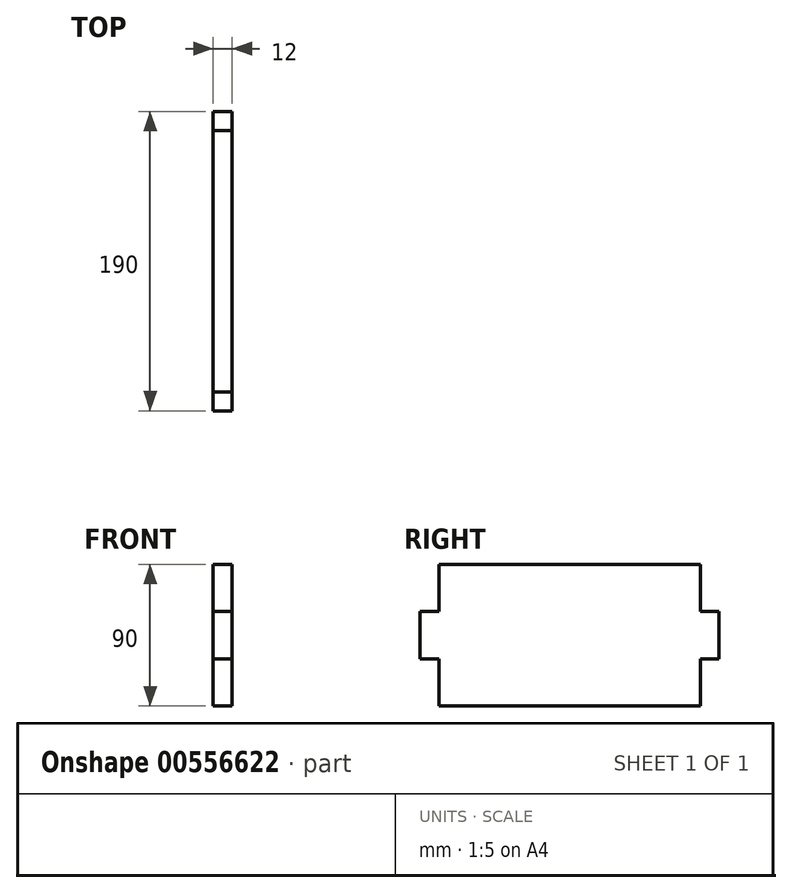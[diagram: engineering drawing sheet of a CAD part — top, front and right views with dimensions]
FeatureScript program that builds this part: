
annotation { "Feature Type Name" : "Feature", "Feature Type Description" : "" }
export const myFeature = defineFeature(function(context is Context, id is Id, definition is map)
    precondition{}
    {
        {
            var Q0;
            Q0=qCreatedBy(makeId("Right.planeOp"),FACE);
            var sketch = newSketch(context, id + "F0", { "sketchPlane" : qUnion([Q0])});
            skLineSegment(sketch, "E0", {"start": v(0, 0) * mm, "end": v(0, 30) * mm});
            skLineSegment(sketch, "E1", {"start": v(0, 30) * mm, "end": v(-12, 30) * mm});
            skLineSegment(sketch, "E2", {"start": v(-12, 30) * mm, "end": v(-12, 60) * mm});
            skLineSegment(sketch, "E3", {"start": v(-12, 60) * mm, "end": v(0, 60) * mm});
            skLineSegment(sketch, "E4", {"start": v(0, 60) * mm, "end": v(0, 90) * mm});
            skLineSegment(sketch, "E5", {"start": v(0, 90) * mm, "end": v(83, 90) * mm});
            skLineSegment(sketch, "E6", {"start": v(83, 90) * mm, "end": v(83, 0) * mm, "construction": true});
            skLineSegment(sketch, "E7", {"start": v(83, 0) * mm, "end": v(0, 0) * mm});
            skLineSegment(sketch, "E8.MirrorCS", {"start": v(166, 30) * mm, "end": v(178, 30) * mm});
            skLineSegment(sketch, "E9.MirrorCS", {"start": v(178, 30) * mm, "end": v(178, 60) * mm});
            skLineSegment(sketch, "E10.MirrorCS", {"start": v(178, 60) * mm, "end": v(166, 60) * mm});
            skLineSegment(sketch, "E11.MirrorCS", {"start": v(83, 0) * mm, "end": v(166, 0) * mm});
            skLineSegment(sketch, "E12.MirrorCS", {"start": v(166, 60) * mm, "end": v(166, 90) * mm});
            skLineSegment(sketch, "E13.MirrorCS", {"start": v(166, 0) * mm, "end": v(166, 30) * mm});
            skLineSegment(sketch, "E14.MirrorCS", {"start": v(166, 90) * mm, "end": v(83, 90) * mm});
            skSolve(sketch);
        }
        {
            var Q0;
            Q0=makeQuery(id+"F0.imprint","IMPRINT",FACE,{"disambiguationData":[TD([[makeQuery(id+"F0.imprint","IMPRINT",EDGE,{"derivedFrom":sQuery(id+"F0.wireOp",EDGE,"E0")}),-1.0]])]});
            extrude(context, id + "F1", {"entities" : qUnion([Q0]), "endBound" : BoundingType.SYMMETRIC, "depth" : 12 * mm, "offsetDistance" : 25 * mm});
        }
    });
